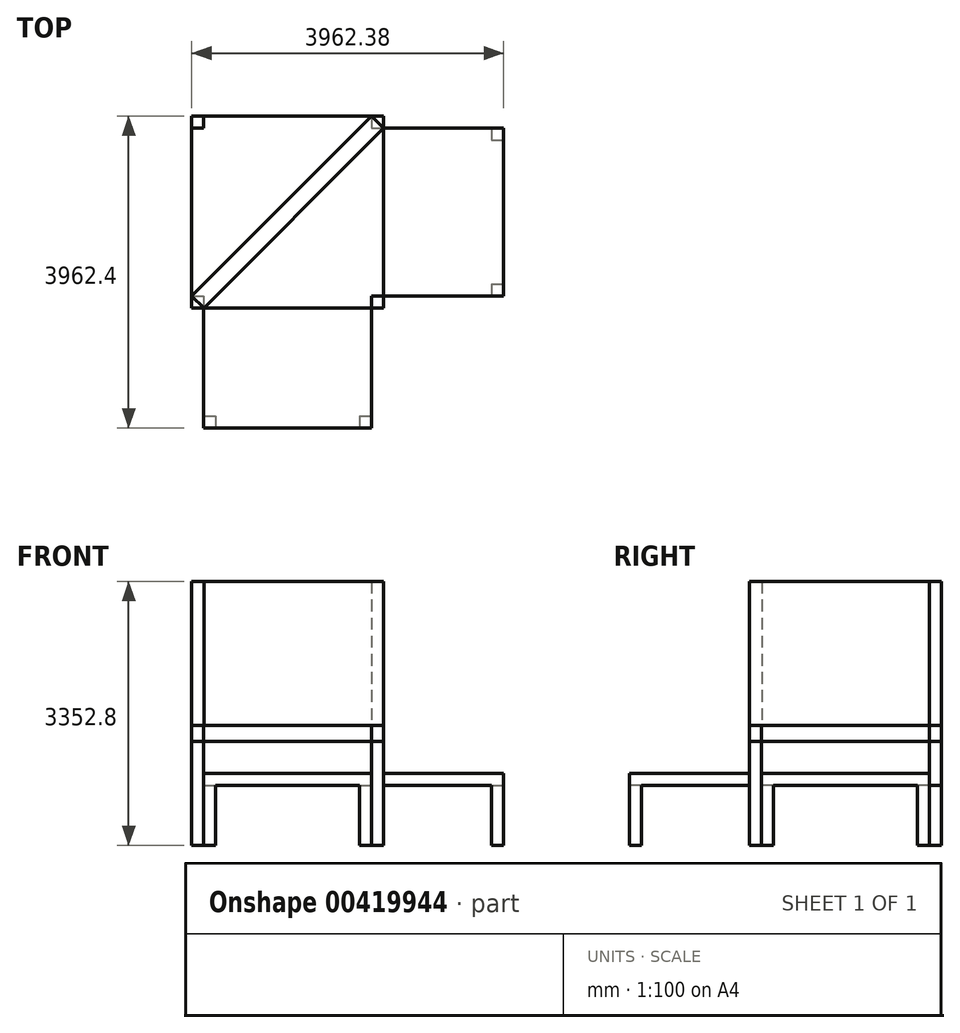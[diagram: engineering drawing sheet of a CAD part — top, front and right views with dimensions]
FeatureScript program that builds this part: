
annotation { "Feature Type Name" : "Feature", "Feature Type Description" : "" }
export const myFeature = defineFeature(function(context is Context, id is Id, definition is map)
    precondition{}
    {
        {
            var Q0;
            Q0=qCreatedBy(makeId("Top.planeOp"),FACE);
            var sketch = newSketch(context, id + "F0", { "sketchPlane" : qUnion([Q0])});
            skLineSegment(sketch, "E0.bottom", {"start": v(-1827.29, 673.2) * mm, "end": v(611.11, 673.2) * mm});
            skLineSegment(sketch, "E0.top", {"start": v(-1827.29, -1765.2) * mm, "end": v(611.11, -1765.2) * mm});
            skLineSegment(sketch, "E0.left", {"start": v(-1827.29, 673.2) * mm, "end": v(-1827.29, -1765.2) * mm});
            skLineSegment(sketch, "E0.right", {"start": v(611.11, 673.2) * mm, "end": v(611.11, -1765.2) * mm});
            skSolve(sketch);
        }
        {
            var Q0;
            Q0=makeQuery(id+"F0.imprint","IMPRINT",FACE,{"disambiguationData":[TD([[makeQuery(id+"F0.imprint","IMPRINT",EDGE,{"derivedFrom":sQuery(id+"F0.wireOp",EDGE,"E0.bottom")}),-1.0]])]});
            var sketch = newSketch(context, id + "F1", { "sketchPlane" : qUnion([Q0])});
            skLineSegment(sketch, "E1.bottom", {"start": v(-1827.29, 673.2) * mm, "end": v(-1674.89, 673.2) * mm});
            skLineSegment(sketch, "E1.top", {"start": v(-1827.29, 520.8) * mm, "end": v(-1674.89, 520.8) * mm});
            skLineSegment(sketch, "E1.left", {"start": v(-1827.29, 673.2) * mm, "end": v(-1827.29, 520.8) * mm});
            skLineSegment(sketch, "E1.right", {"start": v(-1674.89, 673.2) * mm, "end": v(-1674.89, 520.8) * mm});
            skLineSegment(sketch, "E2.bottom", {"start": v(-1827.29, -1612.8) * mm, "end": v(-1674.89, -1612.8) * mm});
            skLineSegment(sketch, "E2.top", {"start": v(-1827.29, -1765.2) * mm, "end": v(-1674.89, -1765.2) * mm});
            skLineSegment(sketch, "E2.left", {"start": v(-1827.29, -1612.8) * mm, "end": v(-1827.29, -1765.2) * mm});
            skLineSegment(sketch, "E2.right", {"start": v(-1674.89, -1612.8) * mm, "end": v(-1674.89, -1765.2) * mm});
            skLineSegment(sketch, "E3.bottom", {"start": v(458.71, -1612.8) * mm, "end": v(611.11, -1612.8) * mm});
            skLineSegment(sketch, "E3.top", {"start": v(458.71, -1765.2) * mm, "end": v(611.11, -1765.2) * mm});
            skLineSegment(sketch, "E3.left", {"start": v(458.71, -1612.8) * mm, "end": v(458.71, -1765.2) * mm});
            skLineSegment(sketch, "E3.right", {"start": v(611.11, -1612.8) * mm, "end": v(611.11, -1765.2) * mm});
            skLineSegment(sketch, "E4.bottom", {"start": v(458.71, 673.2) * mm, "end": v(611.11, 673.2) * mm});
            skLineSegment(sketch, "E4.top", {"start": v(458.71, 520.8) * mm, "end": v(611.11, 520.8) * mm});
            skLineSegment(sketch, "E4.left", {"start": v(458.71, 673.2) * mm, "end": v(458.71, 520.8) * mm});
            skLineSegment(sketch, "E4.right", {"start": v(611.11, 673.2) * mm, "end": v(611.11, 520.8) * mm});
            skSolve(sketch);
        }
        {
            var Q0;
            Q0=qSketchRegion(id+"F1",true);
            extrude(context, id + "F2", {"entities" : qUnion([Q0]), "oppositeDirection" : true, "depth" : 1524 * mm, "offsetDistance" : 25.4 * mm});
        }
        {
            var Q0;
            Q0=qSketchRegion(id+"F0",true);
            extrude(context, id + "F3", {"entities" : qUnion([Q0]), "oppositeDirection" : true, "depth" : 203.2 * mm, "offsetDistance" : 25.4 * mm});
        }
        {
            var Q0;
            Q0=makeQuery(id+"F3.opExtrude","CAP_FACE",FACE,{"disambiguationData":[OSD([sQuery(id+"F0.wireOp",EDGE,"E0.bottom"),sQuery(id+"F0.wireOp",EDGE,"E0.top"),sQuery(id+"F0.wireOp",EDGE,"E0.left"),sQuery(id+"F0.wireOp",EDGE,"E0.right")])],"isStart":true});
            var sketch = newSketch(context, id + "F4", { "sketchPlane" : qUnion([Q0])});
            skLineSegment(sketch, "E5", {"start": v(-1827.29, -1611.4) * mm, "end": v(457.14, 673.2) * mm});
            skLineSegment(sketch, "E6", {"start": v(457.14, 673.2) * mm, "end": v(611.11, 519.23) * mm});
            skLineSegment(sketch, "E7", {"start": v(611.11, 519.23) * mm, "end": v(-1673.16, -1765.2) * mm});
            skLineSegment(sketch, "E8", {"start": v(-1673.16, -1765.2) * mm, "end": v(-1827.29, -1611.4) * mm});
            skSolve(sketch);
        }
        {
            var Q0;
            {var subQ0=sQuery(id+"F0.wireOp",EDGE,"E0.right");var subQ1=sQuery(id+"F0.wireOp",EDGE,"E0.top");var subQ2=makeQuery(id+"F3.opExtrude","CAP_FACE",FACE,{"disambiguationData":[OSD([sQuery(id+"F0.wireOp",EDGE,"E0.bottom"),subQ1,sQuery(id+"F0.wireOp",EDGE,"E0.left"),subQ0])],"isStart":true});Q0=makeQuery(id+"F3KuQgcsKrN1SjG_5.boolean.opBoolean","SPLIT",FACE,{"disambiguationData":[TD([subQ2,makeQuery(id+"F3.opExtrude","SWEPT_FACE",FACE,{"disambiguationData":[OSD([subQ1])]}),makeQuery(id+"F3.opExtrude","SWEPT_FACE",FACE,{"disambiguationData":[OSD([subQ0])]}),makeQuery(id+"F3KuQgcsKrN1SjG_5.opExtrude","SWEPT_FACE",FACE,{"disambiguationData":[OSD([sQuery(id+"F4.wireOp",EDGE,"E6")])]}),makeQuery(id+"F3KuQgcsKrN1SjG_5.opExtrude","SWEPT_FACE",FACE,{"disambiguationData":[OSD([sQuery(id+"F4.wireOp",EDGE,"E7")])]}),makeQuery(id+"F3KuQgcsKrN1SjG_5.opExtrude","SWEPT_FACE",FACE,{"disambiguationData":[OSD([sQuery(id+"F4.wireOp",EDGE,"E8")])]})])],"derivedFrom":subQ2});}
            var sketch = newSketch(context, id + "F5", { "sketchPlane" : qUnion([Q0])});
            skLineSegment(sketch, "E9.bottom", {"start": v(458.71, -3289.2) * mm, "end": v(-1674.89, -3289.2) * mm});
            skLineSegment(sketch, "E9.top", {"start": v(458.71, -1765.2) * mm, "end": v(-1674.89, -1765.2) * mm});
            skLineSegment(sketch, "E9.left", {"start": v(458.71, -3289.2) * mm, "end": v(458.71, -1765.2) * mm});
            skLineSegment(sketch, "E9.right", {"start": v(-1674.89, -3289.2) * mm, "end": v(-1674.89, -1765.2) * mm});
            skLineSegment(sketch, "E10", {"start": v(611.11, -1765.2) * mm, "end": v(-1826.07, 671.66) * mm});
            skLineSegment(sketch, "E11.MirrorCS", {"start": v(2134.82, 520.99) * mm, "end": v(610.82, 520.8) * mm});
            skLineSegment(sketch, "E12.MirrorCS", {"start": v(2135.1, -1612.61) * mm, "end": v(2134.82, 520.99) * mm});
            skLineSegment(sketch, "E13.MirrorCS", {"start": v(2135.1, -1612.61) * mm, "end": v(611.1, -1612.8) * mm});
            skLineSegment(sketch, "E14.MirrorCS", {"start": v(611.1, -1612.8) * mm, "end": v(610.82, 520.8) * mm});
            skSolve(sketch);
        }
        {
            var Q0;
            Q0 = qSketchRegion(id + "F5", true);
            extrude(context, id + "F6", {"entities" : qUnion([Q0]), "oppositeDirection" : true, "depth" : 1524 * mm, "offsetDistance" : 25.4 * mm});
        }
        {
            var Q0;
            Q0=makeQuery(id+"F6.opExtrude","SWEPT_FACE",FACE,{"disambiguationData":[OSD([sQuery(id+"F5.wireOp",EDGE,"E9.bottom")])]});
            var sketch = newSketch(context, id + "F7", { "sketchPlane" : qUnion([Q0])});
            skLineSegment(sketch, "E15.bottom", {"start": v(-1674.89, 0) * mm, "end": v(458.71, 0) * mm});
            skLineSegment(sketch, "E15.top", {"start": v(-1674.89, -609.6) * mm, "end": v(458.71, -609.6) * mm});
            skLineSegment(sketch, "E15.left", {"start": v(-1674.89, 0) * mm, "end": v(-1674.89, -609.6) * mm});
            skLineSegment(sketch, "E15.right", {"start": v(458.71, 0) * mm, "end": v(458.71, -609.6) * mm});
            skLineSegment(sketch, "E16.bottom", {"start": v(-1522.49, -762) * mm, "end": v(306.31, -762) * mm});
            skLineSegment(sketch, "E16.top", {"start": v(-1522.49, -1524) * mm, "end": v(306.31, -1524) * mm});
            skLineSegment(sketch, "E16.left", {"start": v(-1522.49, -762) * mm, "end": v(-1522.49, -1524) * mm});
            skLineSegment(sketch, "E16.right", {"start": v(306.31, -762) * mm, "end": v(306.31, -1524) * mm});
            skSolve(sketch);
        }
        {
            var Q0;
            Q0 = qSketchRegion(id + "F7", true);
            extrude(context, id + "F8", {"entities" : qUnion([Q0]), "operationType" : NewBodyOperationType.REMOVE, "endBound" : BoundingType.UP_TO_NEXT, "oppositeDirection" : true, "depth" : 1397 * mm, "offsetDistance" : 25.4 * mm});
        }
        {
            var Q0;
            Q0=makeQuery(id+"F6.opExtrude","SWEPT_FACE",FACE,{"disambiguationData":[OSD([sQuery(id+"F5.wireOp",EDGE,"E9.left")])]});
            var sketch = newSketch(context, id + "F9", { "sketchPlane" : qUnion([Q0])});
            skLineSegment(sketch, "E17.bottom", {"start": v(-3136.8, -1524) * mm, "end": v(-1765.2, -1524) * mm});
            skLineSegment(sketch, "E17.top", {"start": v(-3136.8, -762) * mm, "end": v(-1765.2, -762) * mm});
            skLineSegment(sketch, "E17.left", {"start": v(-3136.8, -1524) * mm, "end": v(-3136.8, -762) * mm});
            skLineSegment(sketch, "E17.right", {"start": v(-1765.2, -1524) * mm, "end": v(-1765.2, -762) * mm});
            skSolve(sketch);
        }
        {
            var Q0;
            Q0=makeQuery(id+"F9.imprint","IMPRINT",FACE,{"disambiguationData":[TD([[makeQuery(id+"F9.imprint","IMPRINT",EDGE,{"derivedFrom":sQuery(id+"F9.wireOp",EDGE,"E17.bottom")}),1.0]])]});
            extrude(context, id + "F10", {"entities" : qUnion([Q0]), "operationType" : NewBodyOperationType.REMOVE, "endBound" : BoundingType.THROUGH_ALL, "oppositeDirection" : true, "depth" : 25.4 * mm, "offsetDistance" : 25.4 * mm});
        }
        {
            var Q0;
            Q0=makeQuery(id+"F6.opExtrude","SWEPT_FACE",FACE,{"disambiguationData":[OSD([sQuery(id+"F5.wireOp",EDGE,"E12.MirrorCS")])]});
            var sketch = newSketch(context, id + "F11", { "sketchPlane" : qUnion([Q0])});
            skLineSegment(sketch, "E18.bottom", {"start": v(-1460.48, -1524) * mm, "end": v(368.32, -1524) * mm});
            skLineSegment(sketch, "E18.top", {"start": v(-1460.48, -762) * mm, "end": v(368.32, -762) * mm});
            skLineSegment(sketch, "E18.left", {"start": v(-1460.48, -1524) * mm, "end": v(-1460.48, -762) * mm});
            skLineSegment(sketch, "E18.right", {"start": v(368.32, -1524) * mm, "end": v(368.32, -762) * mm});
            skLineSegment(sketch, "E19.bottom", {"start": v(-1612.88, 0) * mm, "end": v(520.72, 0) * mm});
            skLineSegment(sketch, "E19.top", {"start": v(-1612.88, -609.6) * mm, "end": v(520.72, -609.6) * mm});
            skLineSegment(sketch, "E19.left", {"start": v(-1612.88, 0) * mm, "end": v(-1612.88, -609.6) * mm});
            skLineSegment(sketch, "E19.right", {"start": v(520.72, 0) * mm, "end": v(520.72, -609.6) * mm});
            skSolve(sketch);
        }
        {
            var Q0;
            Q0=makeQuery(id+"F11.imprint","IMPRINT",FACE,{"disambiguationData":[TD([[makeQuery(id+"F11.imprint","IMPRINT",EDGE,{"derivedFrom":sQuery(id+"F11.wireOp",EDGE,"E18.bottom")}),1.0]])]});
            var Q1;
            Q1 = qSketchRegion(id + "F11", true);
            extrude(context, id + "F12", {"entities" : qUnion([Q0, Q1]), "operationType" : NewBodyOperationType.REMOVE, "endBound" : BoundingType.UP_TO_NEXT, "oppositeDirection" : true, "depth" : 25.4 * mm, "offsetDistance" : 25.4 * mm});
        }
        {
            var Q0;
            Q0=makeQuery(id+"F6.opExtrude","SWEPT_FACE",FACE,{"disambiguationData":[OSD([sQuery(id+"F5.wireOp",EDGE,"E13.MirrorCS")])]});
            var sketch = newSketch(context, id + "F13", { "sketchPlane" : qUnion([Q0])});
            skLineSegment(sketch, "E20.bottom", {"start": v(610.9, -1524) * mm, "end": v(1982.49, -1524) * mm});
            skLineSegment(sketch, "E20.top", {"start": v(610.9, -762) * mm, "end": v(1982.49, -762) * mm});
            skLineSegment(sketch, "E20.left", {"start": v(610.9, -1524) * mm, "end": v(610.9, -762) * mm});
            skLineSegment(sketch, "E20.right", {"start": v(1982.49, -1524) * mm, "end": v(1982.49, -762) * mm});
            skSolve(sketch);
        }
        {
            var Q0;
            Q0=makeQuery(id+"F13.imprint","IMPRINT",FACE,{"disambiguationData":[TD([[makeQuery(id+"F13.imprint","IMPRINT",EDGE,{"derivedFrom":sQuery(id+"F13.wireOp",EDGE,"E20.bottom")}),-1.0]])]});
            var Q1;
            Q1 = qSketchRegion(id + "F13", true);
            extrude(context, id + "F14", {"entities" : qUnion([Q0, Q1]), "operationType" : NewBodyOperationType.REMOVE, "endBound" : BoundingType.THROUGH_ALL, "oppositeDirection" : true, "depth" : 25.4 * mm, "offsetDistance" : 25.4 * mm});
        }
        {
            var Q0;
            Q0=makeQuery(id+"F4.imprint","IMPRINT",FACE,{"disambiguationData":[TD([[makeQuery(id+"F4.imprint","IMPRINT",EDGE,{"derivedFrom":sQuery(id+"F4.wireOp",EDGE,"E5")}),-1.0]])]});
            extrude(context, id + "F15", {"entities" : qUnion([Q0]), "depth" : 1828.8 * mm, "offsetDistance" : 25.4 * mm});
        }
    });
